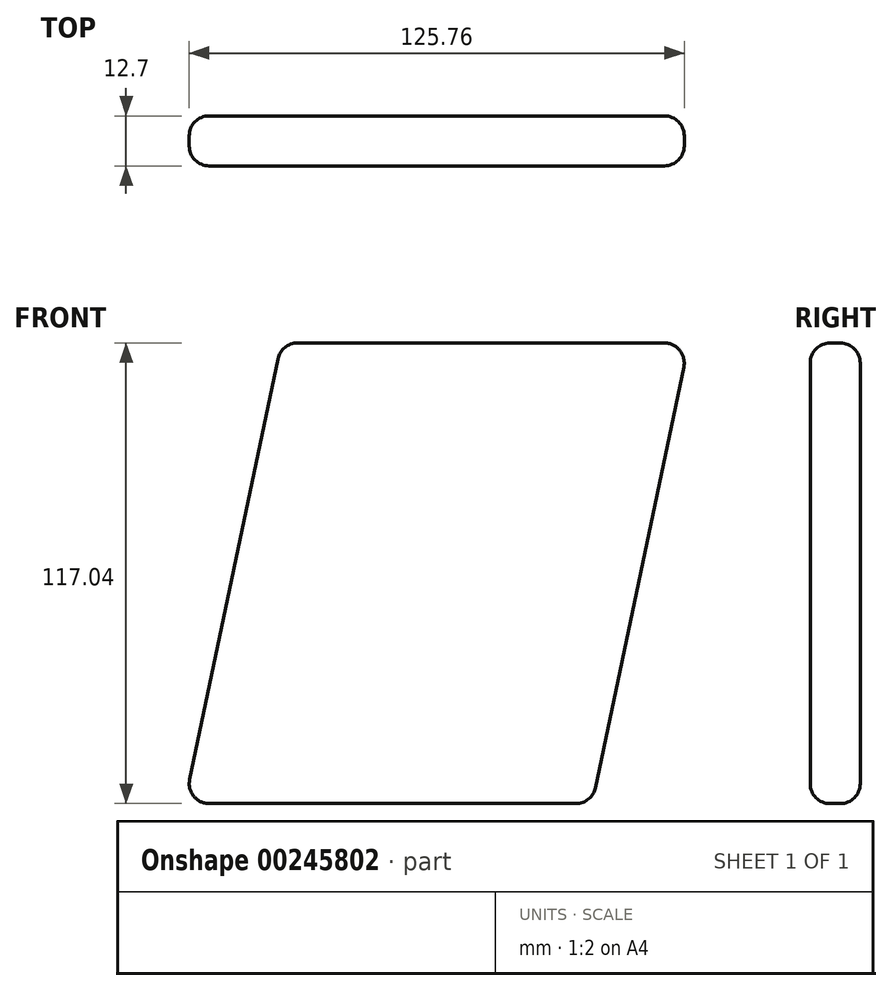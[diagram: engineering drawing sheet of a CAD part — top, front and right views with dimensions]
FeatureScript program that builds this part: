
annotation { "Feature Type Name" : "Feature", "Feature Type Description" : "" }
export const myFeature = defineFeature(function(context is Context, id is Id, definition is map)
    precondition{}
    {
        {
            var Q0;
            Q0=qCreatedBy(makeId("Front.planeOp"),FACE);
            var sketch = newSketch(context, id + "F0", { "sketchPlane" : qUnion([Q0])});
            skLineSegment(sketch, "E0.bottom", {"start": v(64.06, 58.52) * mm, "end": v(-39.5, 58.52) * mm});
            skLineSegment(sketch, "E0.top", {"start": v(39.5, -58.52) * mm, "end": v(-64.06, -58.52) * mm});
            skLineSegment(sketch, "E0.right", {"start": v(-64.06, -58.52) * mm, "end": v(-39.5, 58.52) * mm});
            skPoint(sketch, "E0.middle", {"position": v(0, 0) * mm});
            skLineSegment(sketch, "E1", {"start": v(64.06, 58.52) * mm, "end": v(39.5, -58.52) * mm});
            skSolve(sketch);
        }
        {
            var Q0;
            Q0 = qSketchRegion(id + "F0", true);
            extrude(context, id + "F1", {"entities" : qUnion([Q0]), "depth" : 12.7 * mm});
        }
        {
            var Q0;
            Q0=makeQuery(id+"F1.opExtrude","CAP_EDGE",EDGE,{"disambiguationData":[OSD([sQuery(id+"F0.wireOp",EDGE,"E1")])],"isStart":false});
            var Q1;
            Q1=makeQuery(id+"F1.opExtrude","SWEPT_EDGE",EDGE,{"disambiguationData":[OSD([sQuery(id+"F0.wireOp",EDGE,"E0.top"),sQuery(id+"F0.wireOp",EDGE,"E1")])]});
            var Q2;
            Q2=makeQuery(id+"F1.opExtrude","CAP_EDGE",EDGE,{"disambiguationData":[OSD([sQuery(id+"F0.wireOp",EDGE,"E1")])],"isStart":true});
            var Q3;
            Q3=makeQuery(id+"F1.opExtrude","SWEPT_FACE",FACE,{"disambiguationData":[OSD([sQuery(id+"F0.wireOp",EDGE,"E1")])]});
            var Q4;
            Q4=makeQuery(id+"F1.opExtrude","SWEPT_FACE",FACE,{"disambiguationData":[OSD([sQuery(id+"F0.wireOp",EDGE,"E0.top")])]});
            var Q5;
            Q5=makeQuery(id+"F1.opExtrude","SWEPT_FACE",FACE,{"disambiguationData":[OSD([sQuery(id+"F0.wireOp",EDGE,"E0.bottom")])]});
            var Q6;
            Q6=makeQuery(id+"F1.opExtrude","SWEPT_FACE",FACE,{"disambiguationData":[OSD([sQuery(id+"F0.wireOp",EDGE,"E0.right")])]});
            fillet(context, id + "F2", {"entities" : qUnion([Q0, Q1, Q2, Q3, Q4, Q5, Q6]), "radius" : 5.08 * mm, "tangentPropagation" : true, "allowEdgeOverflow" : false});
        }
    });
